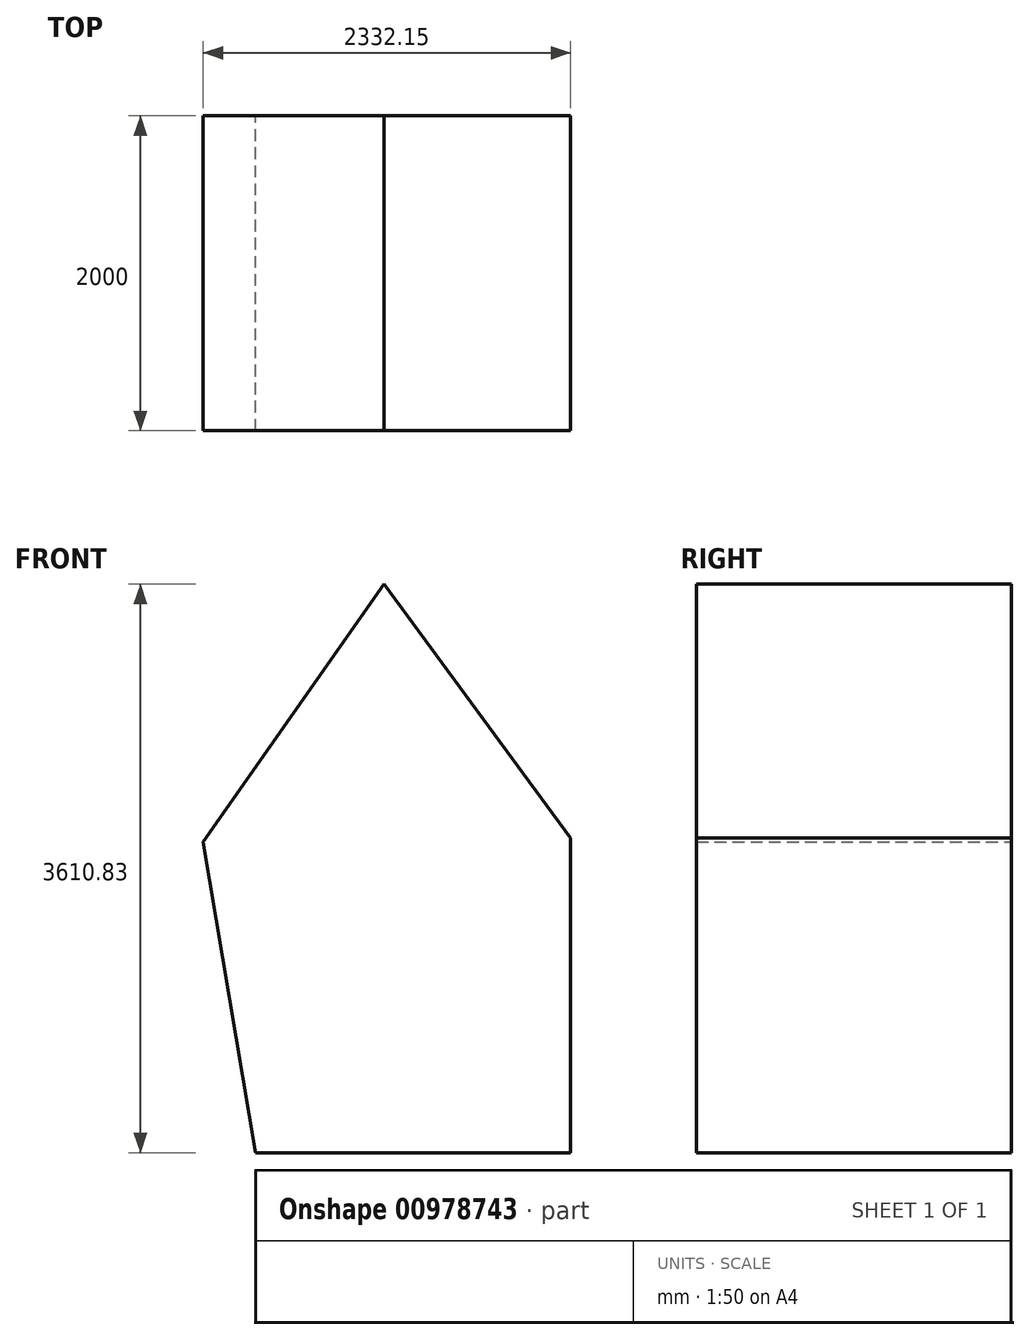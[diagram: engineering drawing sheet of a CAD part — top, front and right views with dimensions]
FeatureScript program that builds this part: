
annotation { "Feature Type Name" : "Feature", "Feature Type Description" : "" }
export const myFeature = defineFeature(function(context is Context, id is Id, definition is map)
    precondition{}
    {
        {
            var Q0;
            Q0=qCreatedBy(makeId("Front.planeOp"),FACE);
            var sketch = newSketch(context, id + "F0", { "sketchPlane" : qUnion([Q0])});
            skLineSegment(sketch, "E0.top", {"start": v(1185.42, -2027.78) * mm, "end": v(-814.58, -2027.78) * mm});
            skPoint(sketch, "E0.middle", {"position": v(0, 0) * mm});
            skLineSegment(sketch, "E1.bottom", {"start": v(-14.75, -1964.9) * mm, "end": v(15.57, -1964.9) * mm});
            skLineSegment(sketch, "E1.top", {"start": v(-14.75, -2027.78) * mm, "end": v(15.57, -2027.78) * mm});
            skLineSegment(sketch, "E1.left", {"start": v(-14.75, -1964.9) * mm, "end": v(-14.75, -2027.78) * mm});
            skLineSegment(sketch, "E1.right", {"start": v(15.57, -1964.9) * mm, "end": v(15.57, -2027.78) * mm});
            skLineSegment(sketch, "E2", {"start": v(-1146.73, -55.55) * mm, "end": v(0, 1583.05) * mm});
            skLineSegment(sketch, "E3", {"start": v(0, 1583.05) * mm, "end": v(1185.42, -27.78) * mm});
            skLineSegment(sketch, "E4", {"start": v(1185.42, -27.78) * mm, "end": v(1185.42, -2027.78) * mm});
            skLineSegment(sketch, "E5", {"start": v(-1146.73, -55.55) * mm, "end": v(-814.58, -2027.78) * mm});
            skSolve(sketch);
        }
        {
            var Q0;
            Q0 = qSketchRegion(id + "F0", true);
            extrude(context, id + "F1", {"entities" : qUnion([Q0]), "depth" : 2000 * mm, "offsetDistance" : 25 * mm});
        }
        {
            var Q0;
            Q0=makeQuery(id+"F1.opExtrude","CAP_FACE",FACE,{"disambiguationData":[OSD([sQuery(id+"F0.wireOp",EDGE,"E0.bottom"),sQuery(id+"F0.wireOp",EDGE,"E0.top"),sQuery(id+"F0.wireOp",EDGE,"E0.left"),sQuery(id+"F0.wireOp",EDGE,"E0.right"),sQuery(id+"F0.wireOp",EDGE,"E1.top"),sQuery(id+"F0.wireOp",EDGE,"E2"),sQuery(id+"F0.wireOp",EDGE,"E3")])],"isStart":false});
            var sketch = newSketch(context, id + "F2", { "sketchPlane" : qUnion([Q0])});
            skLineSegment(sketch, "E6", {"start": v(-1146.73, -55.55) * mm, "end": v(-1157.9, -65.66) * mm});
            skLineSegment(sketch, "E7", {"start": v(-1157.9, -65.66) * mm, "end": v(-1157.9, -55.55) * mm});
            skLineSegment(sketch, "E8", {"start": v(-1157.9, -55.55) * mm, "end": v(-1146.73, -55.55) * mm});
            skSolve(sketch);
        }
        {
            var Q0;
            Q0 = qSketchRegion(id + "F2", true);
            extrude(context, id + "F3", {"entities" : qUnion([Q0]), "operationType" : NewBodyOperationType.REMOVE, "oppositeDirection" : true, "depth" : 39.7 * mm, "offsetDistance" : 25 * mm});
        }
        {
            var Q0;
            Q0=makeQuery(id+"F1.opExtrude","CAP_FACE",FACE,{"disambiguationData":[OSD([sQuery(id+"F0.wireOp",EDGE,"E0.bottom"),sQuery(id+"F0.wireOp",EDGE,"E0.top"),sQuery(id+"F0.wireOp",EDGE,"E0.left"),sQuery(id+"F0.wireOp",EDGE,"E0.right"),sQuery(id+"F0.wireOp",EDGE,"E1.top"),sQuery(id+"F0.wireOp",EDGE,"E2"),sQuery(id+"F0.wireOp",EDGE,"E3")])],"isStart":true});
            var sketch = newSketch(context, id + "F4", { "sketchPlane" : qUnion([Q0])});
            skLineSegment(sketch, "E9", {"start": v(0, 1583.05) * mm, "end": v(-11.18, 1572.33) * mm});
            skLineSegment(sketch, "E10", {"start": v(-11.18, 1572.33) * mm, "end": v(-11.18, 1583.05) * mm});
            skLineSegment(sketch, "E11", {"start": v(-11.18, 1583.05) * mm, "end": v(0, 1583.05) * mm});
            skSolve(sketch);
        }
        {
            var Q0;
            Q0 = qSketchRegion(id + "F4", true);
            extrude(context, id + "F5", {"entities" : qUnion([Q0]), "operationType" : NewBodyOperationType.REMOVE, "oppositeDirection" : true, "depth" : 25 * mm, "offsetDistance" : 25 * mm});
        }
    });
